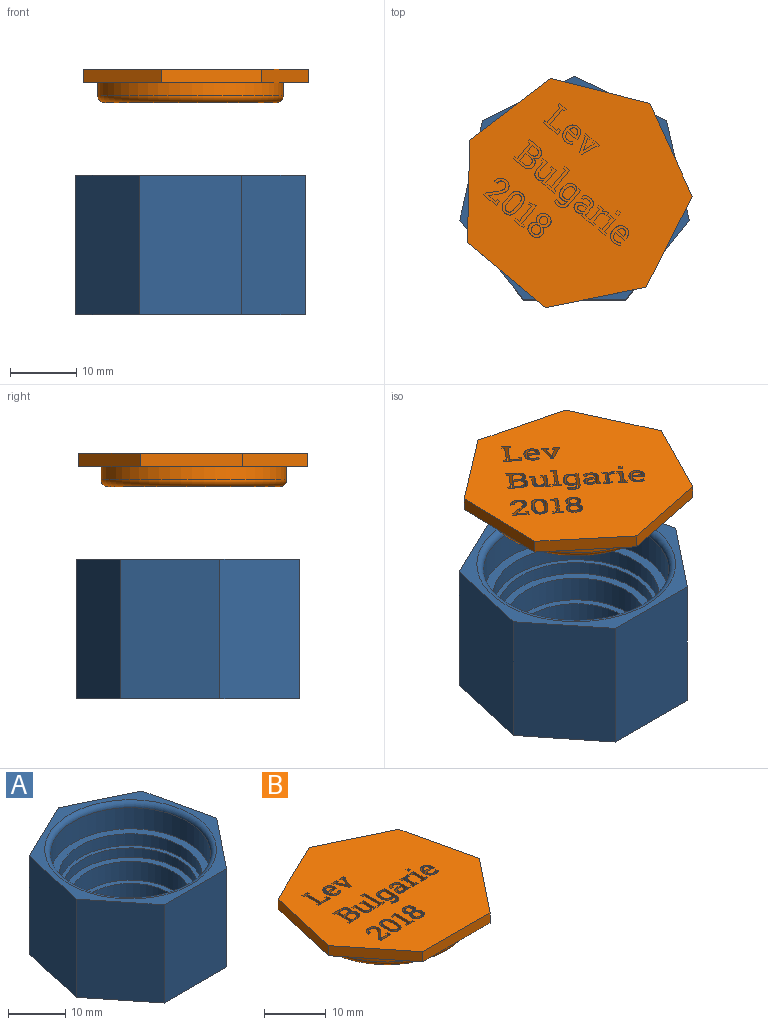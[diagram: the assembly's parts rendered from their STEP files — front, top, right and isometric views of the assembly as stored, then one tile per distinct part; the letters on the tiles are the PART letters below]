
ASSEMBLY  parts=2 mates=1
PART A: 22 faces, bbox 34.6x34x21 mm
  f0: plane 17x17mm, normal (0,0,1), area 227mm2, adj f1
  f1: cylinder r=8.5mm len=17mm, axis (0,0,-1), area 106.8mm2, adj f0,f2
  f2: plane 19x19mm, normal (0,0,1), area 56.5mm2, adj f1,f3
  f3: cylinder r=9.5mm len=19mm, axis (0,0,-1), area 238.8mm2, adj f2,f4
  f4: plane 21x21mm, normal (0,0,1), area 62.8mm2, adj f3,f5
  f5: cylinder r=10.5mm len=21mm, axis (0,0,-1), area 263.9mm2, adj f4,f6
  f6: plane 23.5x23.5mm, normal (0,0,1), area 87.4mm2, adj f5,f7
  f7: cylinder r=11.75mm len=23.5mm, axis (0,0,-1), area 147.7mm2, adj f6,f8
  f8: plane 25x25mm, normal (0,0,1), area 57.1mm2, adj f7,f9
  f9: cylinder r=12.5mm len=25mm, axis (0,0,-1), area 196.3mm2, adj f8,f10
  f10: plane 28x28mm, normal (0,0,1), area 124.9mm2, adj f9,f17
  f11: plane 21x12.05mm, normal (-0.78,-0.62,0), area 323.6mm2, adj f12,f18,f19,f20
  f12: plane 21x15.41mm, normal (0,-1,0), area 323.6mm2, adj f11,f13,f19,f20
  f13: plane 21x12.05mm, normal (0.78,-0.62,0), area 323.6mm2, adj f12,f14,f19,f20
  f14: plane 21x15.02mm, normal (0.97,0.22,0), area 323.6mm2, adj f13,f15,f19,f20
  f15: plane 21x13.88mm, normal (0.43,0.9,0), area 323.6mm2, adj f14,f16,f19,f20
  f16: plane 21x13.88mm, normal (-0.43,0.9,0), area 323.6mm2, adj f15,f18,f19,f20
  f17: cylinder r=14mm len=28mm, axis (0,0,-1), area 395.8mm2, adj f10,f21
  f18: plane 21x15.02mm, normal (-0.97,0.22,0), area 323.6mm2, adj f11,f16,f19,f20
  f19: plane 34.63x33.76mm, normal (0,0,1), area 156.1mm2, adj f11,f12,f13,f14,f15,f16,f18,f21
  f20: plane 34.63x33.76mm, normal (0,0,-1), area 863mm2, adj f11,f12,f13,f14,f15,f16,f18
  f21: torus R=15mm, axis (0,0,1), area 141.8mm2, adj f17,f19
PART B: 363 faces, bbox 34.6x33.8x5 mm
  f0: plane 34.63x33.76mm, normal (0,0,1), area 793.5mm2, adj f1,f2,f3,f4,f5,f6,f7,f11
  f1: plane 15.41x2mm, normal (0,-1,0), area 30.8mm2, adj f0,f2,f7,f8
  f2: plane 12.05x9.61mm, normal (0.78,-0.62,0), area 30.8mm2, adj f0,f1,f3,f8
  f3: plane 15.02x3.43mm, normal (0.97,0.22,0), area 30.8mm2, adj f0,f2,f4,f8
  f4: plane 13.88x6.69mm, normal (0.43,0.9,0), area 30.8mm2, adj f0,f3,f5,f8
  f5: plane 13.88x6.69mm, normal (-0.43,0.9,0), area 30.8mm2, adj f0,f4,f6,f8
  f6: plane 15.02x3.43mm, normal (-0.97,0.22,0), area 30.8mm2, adj f0,f5,f7,f8
  f7: plane 12.05x9.61mm, normal (-0.78,-0.62,0), area 30.8mm2, adj f0,f1,f6,f8
  f8: plane 34.63x33.76mm, normal (0,0,-1), area 247.2mm2, adj f1,f2,f3,f4,f5,f6,f7,f9
  f9: cylinder r=14mm len=28mm, axis (0,0,1), area 175.9mm2, adj f8,f362
  f10: plane 26x26mm, normal (0,0,-1), area 530.9mm2, adj f362
  f11: plane 2x0.33mm, normal (1,0,0), area 0.7mm2, adj f0,f12,f24,f25
  f12: plane 2.74x2mm, normal (0,1,0), area 5.5mm2, adj f0,f11,f13,f25
  f13: plane 2x0.84mm, normal (-1,0,0), area 1.7mm2, adj f0,f12,f14,f25
  f14: plane 2x0.44mm, normal (0,-1,0), area 0.9mm2, adj f0,f13,f15,f25
  f15: plane 2x0.44mm, normal (1,-0.09,0), area 0.9mm2, adj f0,f14,f16,f25
  f16: plane 2x1.32mm, normal (0,-1,0), area 2.6mm2, adj f0,f15,f17,f25
  f17: plane 3x2mm, normal (-1,0,0), area 6mm2, adj f0,f16,f18,f25
  f18: plane 2x0.43mm, normal (-0.17,0.99,0), area 0.9mm2, adj f0,f17,f19,f25
  f19: plane 2x0.33mm, normal (-1,0,0), area 0.7mm2, adj f0,f18,f20,f25
  f20: plane 2x1.37mm, normal (0,-1,0), area 2.7mm2, adj f0,f19,f21,f25
  f21: plane 2x0.33mm, normal (1,0,0), area 0.7mm2, adj f0,f20,f22,f25
  f22: plane 2x0.43mm, normal (0.17,0.99,0), area 0.9mm2, adj f0,f21,f23,f25
  f23: plane 3x2mm, normal (1,0,0), area 6mm2, adj f0,f22,f24,f25
  f24: plane 2x0.43mm, normal (0.17,-0.99,0), area 0.9mm2, adj f0,f11,f23,f25
  f25: plane 3.81x2.74mm, normal (0,0,1), area 3.4mm2, adj f11,f12,f13,f14,f15,f16,f17,f18
  f26: plane 2x0.35mm, normal (1,0,0), area 0.7mm2, adj f0,f27,f48,f49
  f27: plane 2.47x2mm, normal (0,1,0), area 4.9mm2, adj f0,f26,f28,f49
  f28: plane 2x0.84mm, normal (-1,0,0), area 1.7mm2, adj f0,f27,f29,f49
  f29: plane 2x0.44mm, normal (0,-1,0), area 0.9mm2, adj f0,f28,f30,f49
  f30: plane 2x0.44mm, normal (1,-0.1,0), area 0.9mm2, adj f0,f29,f31,f49
  f31: plane 2x1.35mm, normal (0,-1,0), area 2.7mm2, adj f0,f30,f32,f49
  f32: plane 2x0.01mm, normal (-0.92,-0.4,0), area 0mm2, adj f0,f31,f33,f49
  f33: plane 2x1.09mm, normal (-0.74,0.68,0), area 3mm2, adj f0,f32,f34,f49
  f34: extruded ~2x0.67mm, area 1.7mm2, adj f0,f33,f35,f49
  f35: extruded ~2x0.62mm, area 1.3mm2, adj f0,f34,f36,f49
  f36: extruded ~2x0.76mm, area 1.7mm2, adj f0,f35,f37,f49
  f37: extruded ~2x0.82mm, area 1.8mm2, adj f0,f36,f38,f49
  f38: extruded ~2x0.94mm, area 2mm2, adj f0,f37,f39,f49
  f39: extruded ~2x0.83mm, area 1.8mm2, adj f0,f38,f40,f49
  f40: plane 2x0.02mm, normal (0.95,0.3,0), area 0mm2, adj f0,f39,f41,f49
  f41: plane 2x0.49mm, normal (0,1,0), area 1mm2, adj f0,f40,f42,f49
  f42: extruded ~2x0.57mm, area 1.2mm2, adj f0,f41,f43,f49
  f43: extruded ~2x0.58mm, area 1.3mm2, adj f0,f42,f44,f49
  f44: extruded ~2x0.44mm, area 1mm2, adj f0,f43,f45,f49
  f45: extruded ~2x0.48mm, area 1mm2, adj f0,f44,f46,f49
  f46: extruded ~2x0.45mm, area 0.9mm2, adj f0,f45,f47,f49
  f47: extruded ~2x0.59mm, area 1.5mm2, adj f0,f46,f48,f49
  f48: plane 2x1.39mm, normal (0.74,-0.67,0), area 3.7mm2, adj f0,f26,f47,f49
  f49: plane 3.86x2.53mm, normal (0,0,1), area 3.9mm2, adj f26,f27,f28,f29,f30,f31,f32,f33
  f50: extruded ~2x0.44mm, area 1mm2, adj f51,f73,f74,f355
  f51: extruded ~2x0.48mm, area 1.1mm2, adj f50,f52,f74,f355
  f52: extruded ~2x0.51mm, area 1.1mm2, adj f51,f53,f74,f355
  f53: plane 2x0.07mm, normal (1,0,0), area 0.1mm2, adj f52,f54,f74,f355
  f54: plane 2x1.3mm, normal (0,-1,0), area 2.6mm2, adj f53,f55,f74,f355
  f55: plane 2x0.01mm, normal (-0.92,-0.4,0), area 0mm2, adj f54,f73,f74,f355
  f56: extruded ~2x0.94mm, area 2.1mm2, adj f0,f57,f72,f74
  f57: extruded ~2x0.6mm, area 1.2mm2, adj f0,f56,f58,f74
  f58: extruded ~2x0.4mm, area 0.9mm2, adj f0,f57,f59,f74
  f59: plane 2x0.33mm, normal (-0.86,-0.52,0), area 0.8mm2, adj f0,f58,f60,f74
  f60: extruded ~2x0.34mm, area 0.8mm2, adj f0,f59,f61,f74
  f61: extruded ~2x0.46mm, area 0.9mm2, adj f0,f60,f62,f74
  f62: extruded ~2x0.56mm, area 1.3mm2, adj f0,f61,f63,f74
  f63: extruded ~2x0.67mm, area 1.4mm2, adj f0,f62,f64,f74
  f64: plane 2x0.01mm, normal (-0.85,0.53,0), area 0mm2, adj f0,f63,f65,f74
  f65: plane 2x1.84mm, normal (0,1,0), area 3.7mm2, adj f0,f64,f66,f74
  f66: plane 2x0.32mm, normal (-1,0,0), area 0.6mm2, adj f0,f65,f67,f74
  f67: extruded ~2x0.92mm, area 2mm2, adj f0,f66,f68,f74
  f68: extruded ~2x0.86mm, area 1.9mm2, adj f0,f67,f69,f74
  f69: extruded ~2x0.85mm, area 1.9mm2, adj f0,f68,f70,f74
  f70: extruded ~2x1mm, area 2.2mm2, adj f0,f69,f71,f74
  f71: plane 2x0.12mm, normal (1,0,0), area 0.2mm2, adj f0,f70,f72,f74
  f72: extruded ~2x1.02mm, area 2.2mm2, adj f0,f56,f71,f74
  f73: extruded ~2x0.55mm, area 1.2mm2, adj f50,f55,f74,f355
  f74: plane 2.94x2.37mm, normal (0,0,1), area 3.5mm2, adj f50,f51,f52,f53,f54,f55,f56,f57
  f75: plane 2x0.51mm, normal (0,1,0), area 1mm2, adj f0,f76,f78,f79
  f76: plane 2x0.53mm, normal (-1,0,0), area 1.1mm2, adj f0,f75,f77,f79
  f77: plane 2x0.51mm, normal (0,-1,0), area 1mm2, adj f0,f76,f78,f79
  f78: plane 2x0.53mm, normal (1,0,0), area 1.1mm2, adj f0,f75,f77,f79
  f79: plane 0.53x0.51mm, normal (0,0,1), area 0.3mm2, adj f75,f76,f77,f78
  f80: plane 2x0.43mm, normal (0.17,-0.99,0), area 0.9mm2, adj f0,f81,f89,f90
  f81: plane 2x0.33mm, normal (1,0,0), area 0.7mm2, adj f0,f80,f82,f90
  f82: plane 2x1.37mm, normal (0,1,0), area 2.7mm2, adj f0,f81,f83,f90
  f83: plane 2x0.33mm, normal (-1,0,0), area 0.7mm2, adj f0,f82,f84,f90
  f84: plane 2x0.43mm, normal (-0.17,-0.99,0), area 0.9mm2, adj f0,f83,f85,f90
  f85: plane 2.43x2mm, normal (-1,0,0), area 4.9mm2, adj f0,f84,f86,f90
  f86: plane 2x0.94mm, normal (0,-1,0), area 1.9mm2, adj f0,f85,f87,f90
  f87: plane 2x0.33mm, normal (1,0,0), area 0.7mm2, adj f0,f86,f88,f90
  f88: plane 2x0.43mm, normal (0.17,0.99,0), area 0.9mm2, adj f0,f87,f89,f90
  f89: plane 2.02x2mm, normal (1,0,0), area 4mm2, adj f0,f80,f88,f90
  f90: plane 2.83x1.37mm, normal (0,0,1), area 1.9mm2, adj f80,f81,f82,f83,f84,f85,f86,f87
  f91: extruded ~2x0.74mm, area 1.6mm2, adj f92,f110,f111,f356
  f92: plane 2x1.12mm, normal (1,0,0), area 2.2mm2, adj f91,f93,f111,f356
  f93: extruded ~2x0.75mm, area 1.6mm2, adj f92,f94,f111,f356
  f94: extruded ~2x0.52mm, area 1.2mm2, adj f93,f95,f111,f356
  f95: extruded ~2x0.52mm, area 1.2mm2, adj f94,f96,f111,f356
  f96: extruded ~2x0.75mm, area 1.6mm2, adj f95,f97,f111,f356
  f97: plane 2x1.12mm, normal (-1,0,0), area 2.2mm2, adj f96,f98,f111,f356
  f98: extruded ~2x0.74mm, area 1.6mm2, adj f97,f99,f111,f356
  f99: extruded ~2x0.52mm, area 1.2mm2, adj f98,f110,f111,f356
  f100: extruded ~2x1.12mm, area 2.4mm2, adj f0,f101,f109,f111
  f101: plane 2x0.9mm, normal (-1,0,0), area 1.8mm2, adj f0,f100,f102,f111
  f102: extruded ~2x1.12mm, area 2.4mm2, adj f0,f101,f103,f111
  f103: extruded ~2x0.89mm, area 2mm2, adj f0,f102,f104,f111
  f104: extruded ~2x0.88mm, area 2mm2, adj f0,f103,f105,f111
  f105: extruded ~2x1.12mm, area 2.4mm2, adj f0,f104,f106,f111
  f106: plane 2x0.9mm, normal (1,0,0), area 1.8mm2, adj f0,f105,f107,f111
  f107: extruded ~2x1.12mm, area 2.4mm2, adj f0,f106,f108,f111
  f108: extruded ~2x0.89mm, area 2mm2, adj f0,f107,f109,f111
  f109: extruded ~2x0.89mm, area 2mm2, adj f0,f100,f108,f111
  f110: extruded ~2x0.52mm, area 1.2mm2, adj f91,f99,f111,f356
  f111: plane 3.92x2.42mm, normal (0,0,1), area 4.3mm2, adj f91,f92,f93,f94,f95,f96,f97,f98
  f112: plane 2x0.59mm, normal (0.12,-0.99,0), area 1.2mm2, adj f0,f113,f121,f122
  f113: plane 2x0.33mm, normal (1,0,0), area 0.7mm2, adj f0,f112,f114,f122
  f114: plane 2x1.69mm, normal (0,1,0), area 3.4mm2, adj f0,f113,f115,f122
  f115: plane 2x0.33mm, normal (-1,0,0), area 0.7mm2, adj f0,f114,f116,f122
  f116: plane 2x0.59mm, normal (-0.12,-0.99,0), area 1.2mm2, adj f0,f115,f117,f122
  f117: plane 3.4x2mm, normal (-1,0,0), area 6.8mm2, adj f0,f116,f118,f122
  f118: plane 2x1.11mm, normal (0.21,-0.98,0), area 2.3mm2, adj f0,f117,f119,f122
  f119: plane 2x0.32mm, normal (1,0,0), area 0.6mm2, adj f0,f118,f120,f122
  f120: plane 2x0.6mm, normal (-0.02,1,0), area 1.2mm2, adj f0,f119,f121,f122
  f121: plane 2.85x2mm, normal (1,0,0), area 5.7mm2, adj f0,f112,f120,f122
  f122: plane 3.81x1.7mm, normal (0,0,1), area 2.6mm2, adj f112,f113,f114,f115,f116,f117,f118,f119
  f123: extruded ~2x0.47mm, area 1mm2, adj f124,f154,f155,f357
  f124: extruded ~2x0.47mm, area 1mm2, adj f123,f125,f155,f357
  f125: extruded ~2x0.44mm, area 1mm2, adj f124,f126,f155,f357
  f126: extruded ~2x0.45mm, area 1mm2, adj f125,f127,f155,f357
  f127: extruded ~2x0.47mm, area 1mm2, adj f126,f128,f155,f357
  f128: extruded ~2x0.47mm, area 1mm2, adj f127,f129,f155,f357
  f129: extruded ~2x0.44mm, area 1mm2, adj f128,f154,f155,f357
  f130: extruded ~2x0.52mm, area 1.1mm2, adj f131,f152,f155,f156
  f131: extruded ~2x0.51mm, area 1.1mm2, adj f130,f132,f155,f156
  f132: extruded ~2x0.52mm, area 1.1mm2, adj f131,f133,f155,f156
  f133: extruded ~2x0.53mm, area 1.1mm2, adj f132,f134,f155,f156
  f134: extruded ~2x0.51mm, area 1.1mm2, adj f133,f135,f155,f156
  f135: extruded ~2x0.52mm, area 1.1mm2, adj f134,f136,f155,f156
  f136: extruded ~2x0.52mm, area 1.1mm2, adj f135,f152,f155,f156
  f137: extruded ~2x0.52mm, area 1.1mm2, adj f0,f138,f153,f155
  f138: extruded ~2x0.78mm, area 1.7mm2, adj f0,f137,f139,f155
  f139: extruded ~2x0.82mm, area 1.8mm2, adj f0,f138,f140,f155
  f140: extruded ~2x0.82mm, area 1.8mm2, adj f0,f139,f141,f155
  f141: extruded ~2x0.78mm, area 1.7mm2, adj f0,f140,f142,f155
  f142: extruded ~2x0.52mm, area 1.1mm2, adj f0,f141,f143,f155
  f143: extruded ~2x0.45mm, area 1.1mm2, adj f0,f142,f144,f155
  f144: extruded ~2x0.52mm, area 1.3mm2, adj f0,f143,f145,f155
  f145: extruded ~2x0.57mm, area 1.2mm2, adj f0,f144,f146,f155
  f146: extruded ~2x0.81mm, area 1.8mm2, adj f0,f145,f147,f155
  f147: extruded ~2x0.9mm, area 1.9mm2, adj f0,f146,f148,f155
  f148: extruded ~2x0.89mm, area 1.9mm2, adj f0,f147,f149,f155
  f149: extruded ~2x0.81mm, area 1.8mm2, adj f0,f148,f150,f155
  f150: extruded ~2x0.57mm, area 1.2mm2, adj f0,f149,f151,f155
  f151: extruded ~2x0.53mm, area 1.3mm2, adj f0,f150,f153,f155
  f152: extruded ~2x0.52mm, area 1.1mm2, adj f130,f136,f155,f156
  f153: extruded ~2x0.45mm, area 1.1mm2, adj f0,f137,f151,f155
  f154: extruded ~2x0.45mm, area 1mm2, adj f123,f129,f155,f357
  f155: plane 3.92x2.48mm, normal (0,0,1), area 4.8mm2, adj f123,f124,f125,f126,f127,f128,f129,f130
  f156: plane 1.45x1.41mm, normal (0,0,1), area 1.6mm2, adj f130,f131,f132,f133,f134,f135,f136,f152
  f157: extruded ~2x0.44mm, area 1mm2, adj f158,f180,f181,f358
  f158: extruded ~2x0.48mm, area 1.1mm2, adj f157,f159,f181,f358
  f159: extruded ~2x0.51mm, area 1.1mm2, adj f158,f160,f181,f358
  f160: plane 2x0.07mm, normal (1,0,0), area 0.1mm2, adj f159,f161,f181,f358
  f161: plane 2x1.3mm, normal (0,-1,0), area 2.6mm2, adj f160,f162,f181,f358
  f162: plane 2x0.01mm, normal (-0.92,-0.4,0), area 0mm2, adj f161,f180,f181,f358
  f163: extruded ~2x0.94mm, area 2.1mm2, adj f0,f164,f179,f181
  f164: extruded ~2x0.6mm, area 1.2mm2, adj f0,f163,f165,f181
  f165: extruded ~2x0.4mm, area 0.9mm2, adj f0,f164,f166,f181
  f166: plane 2x0.33mm, normal (-0.86,-0.52,0), area 0.8mm2, adj f0,f165,f167,f181
  f167: extruded ~2x0.34mm, area 0.8mm2, adj f0,f166,f168,f181
  f168: extruded ~2x0.46mm, area 0.9mm2, adj f0,f167,f169,f181
  f169: extruded ~2x0.56mm, area 1.3mm2, adj f0,f168,f170,f181
  f170: extruded ~2x0.67mm, area 1.4mm2, adj f0,f169,f171,f181
  f171: plane 2x0.01mm, normal (-0.85,0.53,0), area 0mm2, adj f0,f170,f172,f181
  f172: plane 2x1.84mm, normal (0,1,0), area 3.7mm2, adj f0,f171,f173,f181
  f173: plane 2x0.32mm, normal (-1,0,0), area 0.6mm2, adj f0,f172,f174,f181
  f174: extruded ~2x0.92mm, area 2mm2, adj f0,f173,f175,f181
  f175: extruded ~2x0.86mm, area 1.9mm2, adj f0,f174,f176,f181
  f176: extruded ~2x0.85mm, area 1.9mm2, adj f0,f175,f177,f181
  f177: extruded ~2x1mm, area 2.2mm2, adj f0,f176,f178,f181
  f178: plane 2x0.12mm, normal (1,0,0), area 0.2mm2, adj f0,f177,f179,f181
  f179: extruded ~2x1.02mm, area 2.2mm2, adj f0,f163,f178,f181
  f180: extruded ~2x0.55mm, area 1.2mm2, adj f157,f162,f181,f358
  f181: plane 2.94x2.37mm, normal (0,0,1), area 3.5mm2, adj f157,f158,f159,f160,f161,f162,f163,f164
  f182: plane 2x0.34mm, normal (-0.15,0.99,0), area 0.7mm2, adj f0,f183,f199,f200
  f183: plane 2x0.33mm, normal (-1,0,0), area 0.7mm2, adj f0,f182,f184,f200
  f184: plane 2x1.09mm, normal (0,-1,0), area 2.2mm2, adj f0,f183,f185,f200
  f185: plane 2x0.33mm, normal (1,0,0), area 0.7mm2, adj f0,f184,f186,f200
  f186: plane 2x0.23mm, normal (0.16,0.99,0), area 0.5mm2, adj f0,f185,f187,f200
  f187: plane 2.46x2mm, normal (0.93,0.36,0), area 5.3mm2, adj f0,f186,f188,f200
  f188: plane 2x0.39mm, normal (0,1,0), area 0.8mm2, adj f0,f187,f189,f200
  f189: plane 2.46x2mm, normal (-0.93,0.36,0), area 5.3mm2, adj f0,f188,f190,f200
  f190: plane 2x0.23mm, normal (-0.16,0.99,0), area 0.5mm2, adj f0,f189,f191,f200
  f191: plane 2x0.33mm, normal (-1,0,0), area 0.7mm2, adj f0,f190,f192,f200
  f192: plane 2x1.09mm, normal (0,-1,0), area 2.2mm2, adj f0,f191,f193,f200
  f193: plane 2x0.33mm, normal (1,0,0), area 0.7mm2, adj f0,f192,f194,f200
  f194: plane 2x0.34mm, normal (0.15,0.99,0), area 0.7mm2, adj f0,f193,f195,f200
  f195: plane 2x1.61mm, normal (0.94,-0.33,0), area 3.4mm2, adj f0,f194,f196,f200
  f196: plane 2x0.2mm, normal (0.97,-0.24,0), area 0.4mm2, adj f0,f195,f197,f200
  f197: plane 2x0.02mm, normal (0,-1,0), area 0mm2, adj f0,f196,f198,f200
  f198: plane 2x0.2mm, normal (-0.97,-0.22,0), area 0.4mm2, adj f0,f197,f199,f200
  f199: plane 2x1.61mm, normal (-0.94,-0.34,0), area 3.4mm2, adj f0,f182,f198,f200
  f200: plane 2.83x2.76mm, normal (0,0,1), area 3mm2, adj f182,f183,f184,f185,f186,f187,f188,f189
  f201: plane 2x0.86mm, normal (0,-1,0), area 1.7mm2, adj f202,f229,f230,f359
  f202: plane 2x1.21mm, normal (-1,0,0), area 2.4mm2, adj f201,f203,f230,f359
  f203: plane 2x0.73mm, normal (0,1,0), area 1.5mm2, adj f202,f204,f230,f359
  f204: extruded ~2x0.56mm, area 1.2mm2, adj f203,f205,f230,f359
  f205: extruded ~2x0.46mm, area 1mm2, adj f204,f206,f230,f359
  f206: extruded ~2x0.43mm, area 1mm2, adj f205,f229,f230,f359
  f207: plane 2x1.38mm, normal (-1,0,0), area 2.8mm2, adj f208,f227,f230,f231
  f208: plane 2x0.97mm, normal (0,1,0), area 1.9mm2, adj f207,f209,f230,f231
  f209: extruded ~2x0.5mm, area 1.1mm2, adj f208,f210,f230,f231
  f210: extruded ~2x0.53mm, area 1.1mm2, adj f209,f211,f230,f231
  f211: extruded ~2x0.49mm, area 1.1mm2, adj f210,f212,f230,f231
  f212: extruded ~2x0.55mm, area 1.2mm2, adj f211,f227,f230,f231
  f213: extruded ~2x0.93mm, area 2mm2, adj f0,f214,f228,f230
  f214: plane 2x1.67mm, normal (0,-1,0), area 3.3mm2, adj f0,f213,f215,f230
  f215: plane 2x0.33mm, normal (1,0,0), area 0.7mm2, adj f0,f214,f216,f230
  f216: plane 2x0.43mm, normal (0.17,0.99,0), area 0.9mm2, adj f0,f215,f217,f230
  f217: plane 3x2mm, normal (1,0,0), area 6mm2, adj f0,f216,f218,f230
  f218: plane 2x0.43mm, normal (0.17,-0.99,0), area 0.9mm2, adj f0,f217,f219,f230
  f219: plane 2x0.33mm, normal (1,0,0), area 0.7mm2, adj f0,f218,f220,f230
  f220: plane 2x1.83mm, normal (0,1,0), area 3.7mm2, adj f0,f219,f221,f230
  f221: extruded ~2x0.92mm, area 2mm2, adj f0,f220,f222,f230
  f222: extruded ~2x0.8mm, area 1.8mm2, adj f0,f221,f223,f230
  f223: extruded ~2x0.61mm, area 1.3mm2, adj f0,f222,f224,f230
  f224: extruded ~2x0.54mm, area 1.3mm2, adj f0,f223,f225,f230
  f225: extruded ~2x0.43mm, area 1mm2, adj f0,f224,f226,f230
  f226: extruded ~2x0.45mm, area 1mm2, adj f0,f225,f228,f230
  f227: plane 2x0.89mm, normal (0,-1,0), area 1.8mm2, adj f207,f212,f230,f231
  f228: extruded ~2x0.77mm, area 1.7mm2, adj f0,f213,f226,f230
  f229: extruded ~2x0.45mm, area 1mm2, adj f201,f206,f230,f359
  f230: plane 3.81x3.09mm, normal (0,0,1), area 5.7mm2, adj f201,f202,f203,f204,f205,f206,f207,f208
  f231: plane 1.63x1.38mm, normal (0,0,1), area 2.1mm2, adj f207,f208,f209,f210,f211,f212,f227
  f232: extruded ~2x0.35mm, area 1mm2, adj f0,f233,f253,f254
  f233: plane 2x0.42mm, normal (1,0.08,0), area 0.8mm2, adj f0,f232,f234,f254
  f234: plane 2x0.79mm, normal (0,1,0), area 1.6mm2, adj f0,f233,f235,f254
  f235: plane 2x0.33mm, normal (-1,0,0), area 0.7mm2, adj f0,f234,f236,f254
  f236: plane 2x0.32mm, normal (-0.22,-0.98,0), area 0.7mm2, adj f0,f235,f237,f254
  f237: plane 2.43x2mm, normal (-1,0,0), area 4.9mm2, adj f0,f236,f238,f254
  f238: plane 2x0.89mm, normal (0,-1,0), area 1.8mm2, adj f0,f237,f239,f254
  f239: plane 2x0.33mm, normal (1,0,0), area 0.7mm2, adj f0,f238,f240,f254
  f240: plane 2x0.38mm, normal (0.19,0.98,0), area 0.8mm2, adj f0,f239,f241,f254
  f241: plane 2x1.63mm, normal (1,0,0), area 3.3mm2, adj f0,f240,f242,f254
  f242: extruded ~2x0.32mm, area 0.8mm2, adj f0,f241,f243,f254
  f243: extruded ~2x0.45mm, area 0.9mm2, adj f0,f242,f244,f254
  f244: extruded ~2x0.42mm, area 0.9mm2, adj f0,f243,f245,f254
  f245: extruded ~2x0.62mm, area 1.3mm2, adj f0,f244,f246,f254
  f246: plane 2x1.67mm, normal (-1,0,0), area 3.3mm2, adj f0,f245,f247,f254
  f247: plane 2x0.84mm, normal (0,-1,0), area 1.7mm2, adj f0,f246,f248,f254
  f248: plane 2x0.33mm, normal (1,0,0), area 0.7mm2, adj f0,f247,f249,f254
  f249: plane 2x0.32mm, normal (0.22,0.98,0), area 0.7mm2, adj f0,f248,f250,f254
  f250: plane 2x1.26mm, normal (1,0,0), area 2.5mm2, adj f0,f249,f251,f254
  f251: extruded ~2x0.92mm, area 2mm2, adj f0,f250,f252,f254
  f252: extruded ~2x0.72mm, area 1.6mm2, adj f0,f251,f253,f254
  f253: extruded ~2x0.49mm, area 1mm2, adj f0,f232,f252,f254
  f254: plane 2.95x2.88mm, normal (0,0,1), area 3.7mm2, adj f232,f233,f234,f235,f236,f237,f238,f239
  f255: plane 2x0.33mm, normal (1,0,0), area 0.7mm2, adj f0,f256,f264,f265
  f256: plane 2x0.43mm, normal (0.17,0.99,0), area 0.9mm2, adj f0,f255,f257,f265
  f257: plane 3.27x2mm, normal (1,0,0), area 6.5mm2, adj f0,f256,f258,f265
  f258: plane 2x0.43mm, normal (0.17,-0.99,0), area 0.9mm2, adj f0,f257,f259,f265
  f259: plane 2x0.33mm, normal (1,0,0), area 0.7mm2, adj f0,f258,f260,f265
  f260: plane 2x1.37mm, normal (0,1,0), area 2.7mm2, adj f0,f259,f261,f265
  f261: plane 2x0.33mm, normal (-1,0,0), area 0.7mm2, adj f0,f260,f262,f265
  f262: plane 2x0.43mm, normal (-0.17,-0.99,0), area 0.9mm2, adj f0,f261,f263,f265
  f263: plane 3.68x2mm, normal (-1,0,0), area 7.4mm2, adj f0,f262,f264,f265
  f264: plane 2x0.94mm, normal (0,-1,0), area 1.9mm2, adj f0,f255,f263,f265
  f265: plane 4.08x1.37mm, normal (0,0,1), area 2.6mm2, adj f255,f256,f257,f258,f259,f260,f261,f262
  f266: extruded ~2x0.69mm, area 1.4mm2, adj f267,f297,f298,f360
  f267: plane 2x0.05mm, normal (-1,0,0), area 0.1mm2, adj f266,f268,f298,f360
  f268: extruded ~2x0.79mm, area 1.6mm2, adj f267,f269,f298,f360
  f269: extruded ~2x0.55mm, area 1.3mm2, adj f268,f270,f298,f360
  f270: extruded ~2x0.38mm, area 0.8mm2, adj f269,f271,f298,f360
  f271: extruded ~2x0.29mm, area 0.8mm2, adj f270,f272,f298,f360
  f272: plane 2x1.3mm, normal (1,0,0), area 2.6mm2, adj f271,f273,f298,f360
  f273: extruded ~2x0.3mm, area 0.8mm2, adj f272,f274,f298,f360
  f274: extruded ~2x0.39mm, area 0.8mm2, adj f273,f297,f298,f360
  f275: extruded ~2x1.1mm, area 2.3mm2, adj f0,f276,f296,f298
  f276: plane 2x0.05mm, normal (1,0,0), area 0.1mm2, adj f0,f275,f277,f298
  f277: extruded ~2x0.99mm, area 2.1mm2, adj f0,f276,f278,f298
  f278: extruded ~2x0.82mm, area 1.9mm2, adj f0,f277,f279,f298
  f279: extruded ~2x0.44mm, area 0.9mm2, adj f0,f278,f280,f298
  f280: extruded ~2x0.33mm, area 0.9mm2, adj f0,f279,f281,f298
  f281: plane 2x0.27mm, normal (1,0,0), area 0.5mm2, adj f0,f280,f282,f298
  f282: extruded ~2x0.55mm, area 1.2mm2, adj f0,f281,f283,f298
  f283: extruded ~2x0.51mm, area 1.1mm2, adj f0,f282,f284,f298
  f284: extruded ~2x0.38mm, area 0.8mm2, adj f0,f283,f285,f298
  f285: extruded ~2x0.34mm, area 0.7mm2, adj f0,f284,f286,f298
  f286: plane 2x0.4mm, normal (0.95,-0.32,0), area 0.8mm2, adj f0,f285,f287,f298
  f287: extruded ~2x0.42mm, area 0.9mm2, adj f0,f286,f288,f298
  f288: extruded ~2x0.44mm, area 0.9mm2, adj f0,f287,f289,f298
  f289: extruded ~2x0.87mm, area 1.9mm2, adj f0,f288,f290,f298
  f290: extruded ~2x0.86mm, area 1.9mm2, adj f0,f289,f291,f298
  f291: plane 2.79x2mm, normal (-1,0,0), area 5.6mm2, adj f0,f290,f292,f298
  f292: plane 2x0.43mm, normal (0,-1,0), area 0.9mm2, adj f0,f291,f293,f298
  f293: plane 2x0.36mm, normal (0.99,-0.13,0), area 0.7mm2, adj f0,f292,f294,f298
  f294: extruded ~2x0.34mm, area 0.9mm2, adj f0,f293,f295,f298
  f295: extruded ~2x0.47mm, area 1mm2, adj f0,f294,f296,f298
  f296: extruded ~2x0.82mm, area 1.9mm2, adj f0,f275,f295,f298
  f297: extruded ~2x0.55mm, area 1.3mm2, adj f266,f274,f298,f360
  f298: plane 4.02x2.41mm, normal (0,0,1), area 4.8mm2, adj f266,f267,f268,f269,f270,f271,f272,f273
  f299: extruded ~2x0.47mm, area 1mm2, adj f300,f333,f334,f361
  f300: extruded ~2x0.35mm, area 0.7mm2, adj f299,f301,f334,f361
  f301: extruded ~2x0.28mm, area 0.6mm2, adj f300,f302,f334,f361
  f302: extruded ~2x0.36mm, area 0.8mm2, adj f301,f303,f334,f361
  f303: extruded ~2x0.5mm, area 1.1mm2, adj f302,f304,f334,f361
  f304: plane 2x0.55mm, normal (0,1,0), area 1.1mm2, adj f303,f305,f334,f361
  f305: plane 2x0.47mm, normal (1,0,0), area 0.9mm2, adj f304,f333,f334,f361
  f306: extruded ~2x0.21mm, area 0.4mm2, adj f0,f307,f332,f334
  f307: plane 2x0.68mm, normal (0,1,0), area 1.4mm2, adj f0,f306,f308,f334
  f308: plane 2x0.33mm, normal (-1,0,0), area 0.7mm2, adj f0,f307,f309,f334
  f309: plane 2x0.21mm, normal (-0.13,-0.99,0), area 0.4mm2, adj f0,f308,f310,f334
  f310: extruded ~2x0.11mm, area 0.2mm2, adj f0,f309,f311,f334
  f311: extruded ~2x0.11mm, area 0.2mm2, adj f0,f310,f312,f334
  f312: plane 2x1.36mm, normal (-1,0,0), area 2.7mm2, adj f0,f311,f313,f334
  f313: extruded ~2x0.7mm, area 1.6mm2, adj f0,f312,f314,f334
  f314: extruded ~2x0.78mm, area 1.7mm2, adj f0,f313,f315,f334
  f315: extruded ~2x0.6mm, area 1.2mm2, adj f0,f314,f316,f334
  f316: extruded ~2x0.47mm, area 1.1mm2, adj f0,f315,f317,f334
  f317: plane 2x0.55mm, normal (1,0,0), area 1.1mm2, adj f0,f316,f318,f334
  f318: plane 2x0.4mm, normal (0,1,0), area 0.8mm2, adj f0,f317,f319,f334
  f319: plane 2x0.3mm, normal (-0.98,0.18,0), area 0.6mm2, adj f0,f318,f320,f334
  f320: extruded ~2x0.24mm, area 0.6mm2, adj f0,f319,f321,f334
  f321: extruded ~2x0.34mm, area 0.7mm2, adj f0,f320,f322,f334
  f322: extruded ~2x0.44mm, area 0.9mm2, adj f0,f321,f323,f334
  f323: extruded ~2x0.39mm, area 0.9mm2, adj f0,f322,f324,f334
  f324: plane 2x0.33mm, normal (1,0,0), area 0.7mm2, adj f0,f323,f325,f334
  f325: plane 2x0.53mm, normal (0,-1,0), area 1.1mm2, adj f0,f324,f326,f334
  f326: extruded ~2x0.89mm, area 1.9mm2, adj f0,f325,f327,f334
  f327: extruded ~2x0.62mm, area 1.5mm2, adj f0,f326,f328,f334
  f328: extruded ~2x0.61mm, area 1.3mm2, adj f0,f327,f329,f334
  f329: extruded ~2x0.67mm, area 1.4mm2, adj f0,f328,f330,f334
  f330: extruded ~2x0.48mm, area 1mm2, adj f0,f329,f331,f334
  f331: extruded ~2x0.37mm, area 1mm2, adj f0,f330,f332,f334
  f332: extruded ~2x0.18mm, area 0.4mm2, adj f0,f306,f331,f334
  f333: extruded ~2x0.3mm, area 0.9mm2, adj f299,f305,f334,f361
  f334: plane 2.94x2.48mm, normal (0,0,1), area 3.8mm2, adj f299,f300,f301,f302,f303,f304,f305,f306
  f335: plane 2x0.33mm, normal (1,0,0), area 0.7mm2, adj f0,f336,f353,f354
  f336: plane 2x0.43mm, normal (0.17,0.99,0), area 0.9mm2, adj f0,f335,f337,f354
  f337: plane 2.02x2mm, normal (1,0,0), area 4mm2, adj f0,f336,f338,f354
  f338: plane 2x0.43mm, normal (0.17,-0.99,0), area 0.9mm2, adj f0,f337,f339,f354
  f339: plane 2x0.33mm, normal (1,0,0), area 0.7mm2, adj f0,f338,f340,f354
  f340: plane 2x1.37mm, normal (0,1,0), area 2.7mm2, adj f0,f339,f341,f354
  f341: plane 2x0.33mm, normal (-1,0,0), area 0.7mm2, adj f0,f340,f342,f354
  f342: plane 2x0.43mm, normal (-0.17,-0.99,0), area 0.9mm2, adj f0,f341,f343,f354
  f343: plane 2x1.62mm, normal (-1,0,0), area 3.2mm2, adj f0,f342,f344,f354
  f344: extruded ~2x0.27mm, area 0.7mm2, adj f0,f343,f345,f354
  f345: extruded ~2x0.34mm, area 0.7mm2, adj f0,f344,f346,f354
  f346: plane 2x0.29mm, normal (0.05,1,0), area 0.6mm2, adj f0,f345,f347,f354
  f347: plane 2x0.48mm, normal (-0.99,0.14,0), area 1mm2, adj f0,f346,f348,f354
  f348: extruded ~2x0.1mm, area 0.2mm2, adj f0,f347,f349,f354
  f349: extruded ~2x0.12mm, area 0.2mm2, adj f0,f348,f350,f354
  f350: extruded ~2x0.4mm, area 0.9mm2, adj f0,f349,f351,f354
  f351: extruded ~2x0.34mm, area 0.9mm2, adj f0,f350,f352,f354
  f352: plane 2x0.41mm, normal (-0.99,-0.12,0), area 0.8mm2, adj f0,f351,f353,f354
  f353: plane 2x0.89mm, normal (0,-1,0), area 1.8mm2, adj f0,f335,f352,f354
  f354: plane 2.88x1.86mm, normal (0,0,1), area 2.3mm2, adj f335,f336,f337,f338,f339,f340,f341,f342
  f355: plane 1.31x0.78mm, normal (0,0,1), area 0.8mm2, adj f50,f51,f52,f53,f54,f55,f73
  f356: plane 3.11x1.39mm, normal (0,0,1), area 3.9mm2, adj f91,f92,f93,f94,f95,f96,f97,f98
  f357: plane 1.29x1.23mm, normal (0,0,1), area 1.3mm2, adj f123,f124,f125,f126,f127,f128,f129,f154
  f358: plane 1.31x0.78mm, normal (0,0,1), area 0.8mm2, adj f157,f158,f159,f160,f161,f162,f180
  f359: plane 1.48x1.21mm, normal (0,0,1), area 1.6mm2, adj f201,f202,f203,f204,f205,f206,f229
  f360: plane 2.1x1.38mm, normal (0,0,1), area 2.5mm2, adj f266,f267,f268,f269,f270,f271,f272,f273
  f361: plane 1.23x0.88mm, normal (0,0,1), area 0.9mm2, adj f299,f300,f301,f302,f303,f304,f305,f333
  f362: torus R=13mm, axis (0,0,1), area 134.6mm2, adj f9,f10
PLACE A at identity fixed
PLACE B rot(axis=(0,0,-1),39.8deg) t=(0,0,37.01)mm
MATE cylindrical A.f17 <-> B.f9  axis (0,0,-1) through (0,0,17.75)mm
